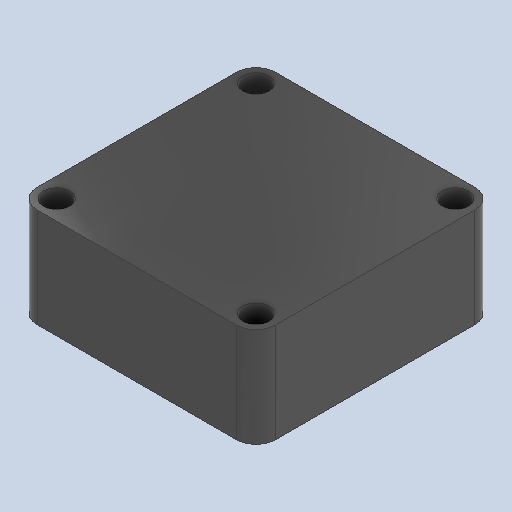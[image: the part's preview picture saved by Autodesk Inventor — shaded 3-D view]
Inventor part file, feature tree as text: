
AUTODESK INVENTOR PART (.ipt)
format: ipt  version: 2025.2 (Build 292293000, 293)  size: 124,416 bytes
history: native  units: mm
features: sketch x2, extrude x1
ambient origin geometry x8: Origin, YZ Plane, XZ Plane, XY Plane, X Axis, Y Axis, Z Axis, Center Point
bodies: Solid1 (feature_tree)
feature tree (3):
  extrude  "Extrusion1"  Depth=36.0mm
  sketch  "Sketch1"  dims[d0=36.0mm d1=36.0mm]
  sketch  "Sketch Circular Pattern1"  dims[d2=4.0mm d3=15.05mm d4=40.0mm d6=360.0deg d8=2.95mm d9=15.0mm d10=0.0mm]
